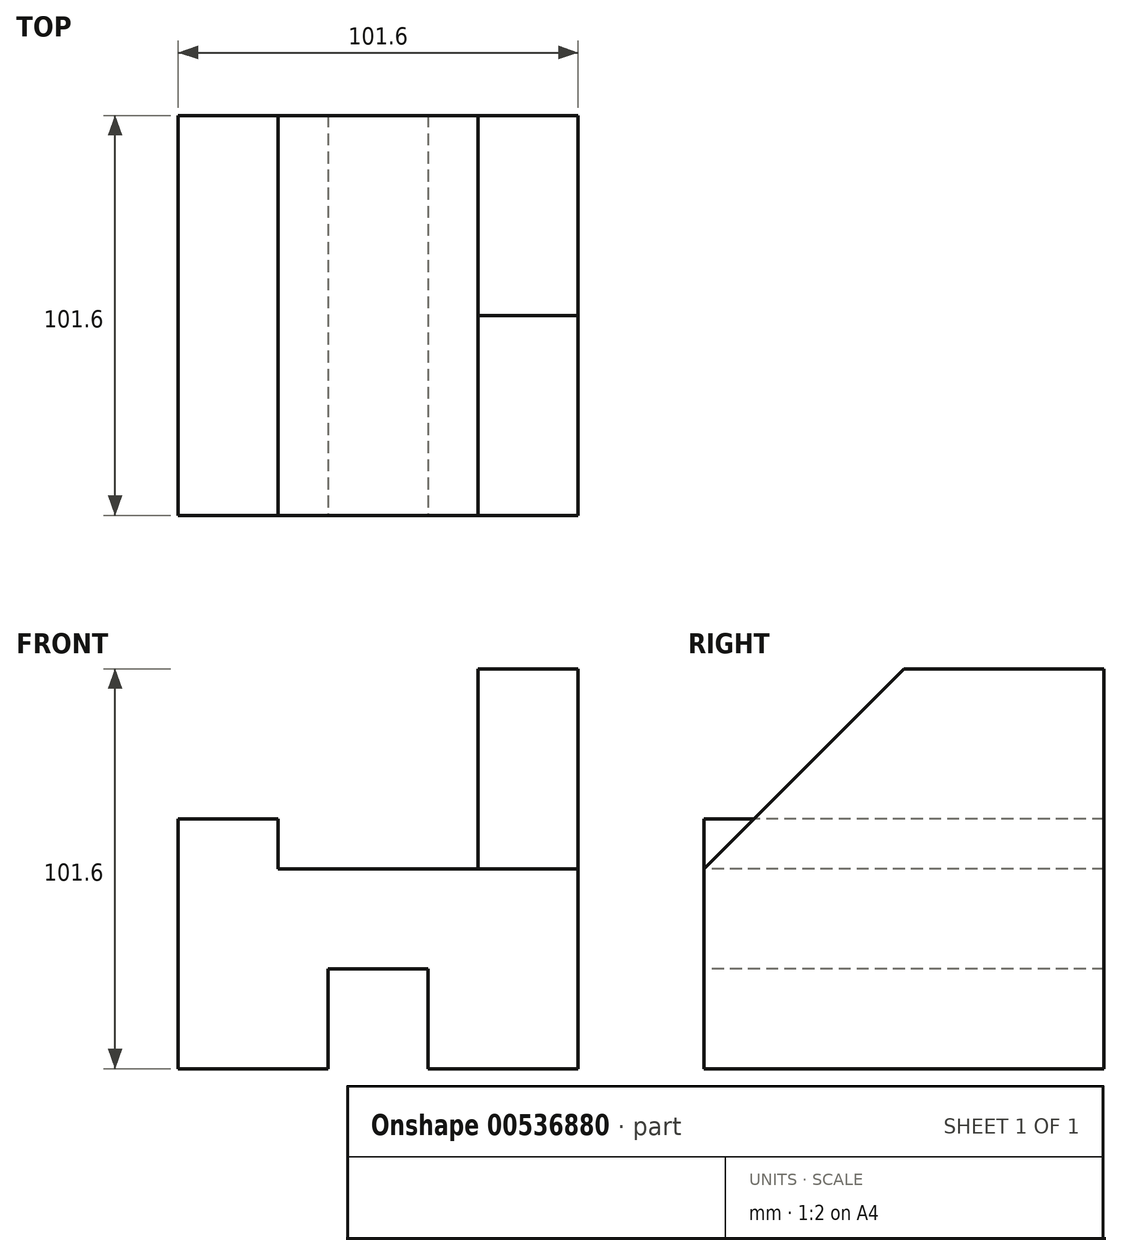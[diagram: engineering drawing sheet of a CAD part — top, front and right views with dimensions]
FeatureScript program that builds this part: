
annotation { "Feature Type Name" : "Feature", "Feature Type Description" : "" }
export const myFeature = defineFeature(function(context is Context, id is Id, definition is map)
    precondition{}
    {
        {
            var Q0;
            Q0=qCreatedBy(makeId("Top.planeOp"),FACE);
            var sketch = newSketch(context, id + "F0", { "sketchPlane" : qUnion([Q0])});
            skLineSegment(sketch, "E0.bottom", {"start": v(0, 0) * mm, "end": v(-101.6, 0) * mm});
            skLineSegment(sketch, "E0.top", {"start": v(0, -101.6) * mm, "end": v(-101.6, -101.6) * mm});
            skLineSegment(sketch, "E0.left", {"start": v(0, 0) * mm, "end": v(0, -101.6) * mm});
            skLineSegment(sketch, "E0.right", {"start": v(-101.6, 0) * mm, "end": v(-101.6, -101.6) * mm});
            skSolve(sketch);
        }
        {
            var Q0;
            Q0=makeQuery(id+"F0.imprint","IMPRINT",FACE,{"disambiguationData":[TD([[makeQuery(id+"F0.imprint","IMPRINT",EDGE,{"derivedFrom":sQuery(id+"F0.wireOp",EDGE,"E0.bottom")}),1.0]])]});
            extrude(context, id + "F1", {"entities" : qUnion([Q0]), "depth" : 101.6 * mm, "offsetDistance" : 25.4 * mm});
        }
        {
            var Q0;
            Q0=makeQuery(id+"F1.opExtrude","SWEPT_FACE",FACE,{"disambiguationData":[OSD([sQuery(id+"F0.wireOp",EDGE,"E0.top")])]});
            var sketch = newSketch(context, id + "F2", { "sketchPlane" : qUnion([Q0])});
            skLineSegment(sketch, "E1", {"start": v(-101.6, 0) * mm, "end": v(-63.5, 0) * mm});
            skLineSegment(sketch, "E2", {"start": v(-63.5, 0) * mm, "end": v(-63.5, 25.4) * mm});
            skLineSegment(sketch, "E3", {"start": v(-63.5, 25.4) * mm, "end": v(-38.1, 25.4) * mm});
            skLineSegment(sketch, "E4", {"start": v(-38.1, 25.4) * mm, "end": v(-38.1, 0) * mm});
            skLineSegment(sketch, "E5.bottom", {"start": v(-101.6, 0) * mm, "end": v(-101.6, 0) * mm});
            skLineSegment(sketch, "E5.top", {"start": v(-101.6, 63.5) * mm, "end": v(-101.6, 63.5) * mm});
            skLineSegment(sketch, "E5.left", {"start": v(-101.6, 0) * mm, "end": v(-101.6, 63.5) * mm});
            skLineSegment(sketch, "E5.right", {"start": v(-101.6, 0) * mm, "end": v(-101.6, 63.5) * mm});
            skLineSegment(sketch, "E6", {"start": v(-101.6, 63.5) * mm, "end": v(-76.2, 63.5) * mm});
            skLineSegment(sketch, "E7", {"start": v(-76.2, 63.5) * mm, "end": v(-76.2, 50.8) * mm});
            skLineSegment(sketch, "E8", {"start": v(-76.2, 50.8) * mm, "end": v(-25.4, 50.8) * mm});
            skLineSegment(sketch, "E9", {"start": v(-25.4, 50.8) * mm, "end": v(-25.4, 101.6) * mm});
            skSolve(sketch);
        }
        {
            var Q0;
            {var subQ1=sQuery(id+"F2.wireOp",EDGE,"E6");Q0=makeQuery(id+"F2.imprint","IMPRINT",FACE,{"disambiguationData":[TD([[makeQuery(id+"F2.imprint","IMPRINT",EDGE,{"derivedFrom":subQ1}),1.0]])]});}
            var Q1;
            {var subQ0=sQuery(id+"F2.wireOp",EDGE,"E2");Q1=makeQuery(id+"F2.imprint","IMPRINT",FACE,{"disambiguationData":[TD([[makeQuery(id+"F2.imprint","IMPRINT",EDGE,{"derivedFrom":subQ0}),-1.0]])]});}
            extrude(context, id + "F3", {"entities" : qUnion([Q0, Q1]), "operationType" : NewBodyOperationType.REMOVE, "oppositeDirection" : true, "depth" : 115.06 * mm, "offsetDistance" : 25.4 * mm});
        }
        {
            var Q0;
            Q0=makeQuery(id+"F1.opExtrude","SWEPT_FACE",FACE,{"disambiguationData":[OSD([sQuery(id+"F0.wireOp",EDGE,"E0.left")])]});
            var sketch = newSketch(context, id + "F4", { "sketchPlane" : qUnion([Q0])});
            skLineSegment(sketch, "E10", {"start": v(-101.6, 50.8) * mm, "end": v(-50.8, 101.6) * mm});
            skSolve(sketch);
        }
        {
            var Q0;
            {var subQ0=sQuery(id+"F4.wireOp",EDGE,"E10");Q0=makeQuery(id+"F4.imprint","IMPRINT",FACE,{"disambiguationData":[TD([[makeQuery(id+"F4.imprint","IMPRINT",EDGE,{"derivedFrom":subQ0}),1.0]])]});}
            extrude(context, id + "F5", {"entities" : qUnion([Q0]), "operationType" : NewBodyOperationType.REMOVE, "oppositeDirection" : true, "depth" : 27.18 * mm, "offsetDistance" : 25.4 * mm});
        }
    });
